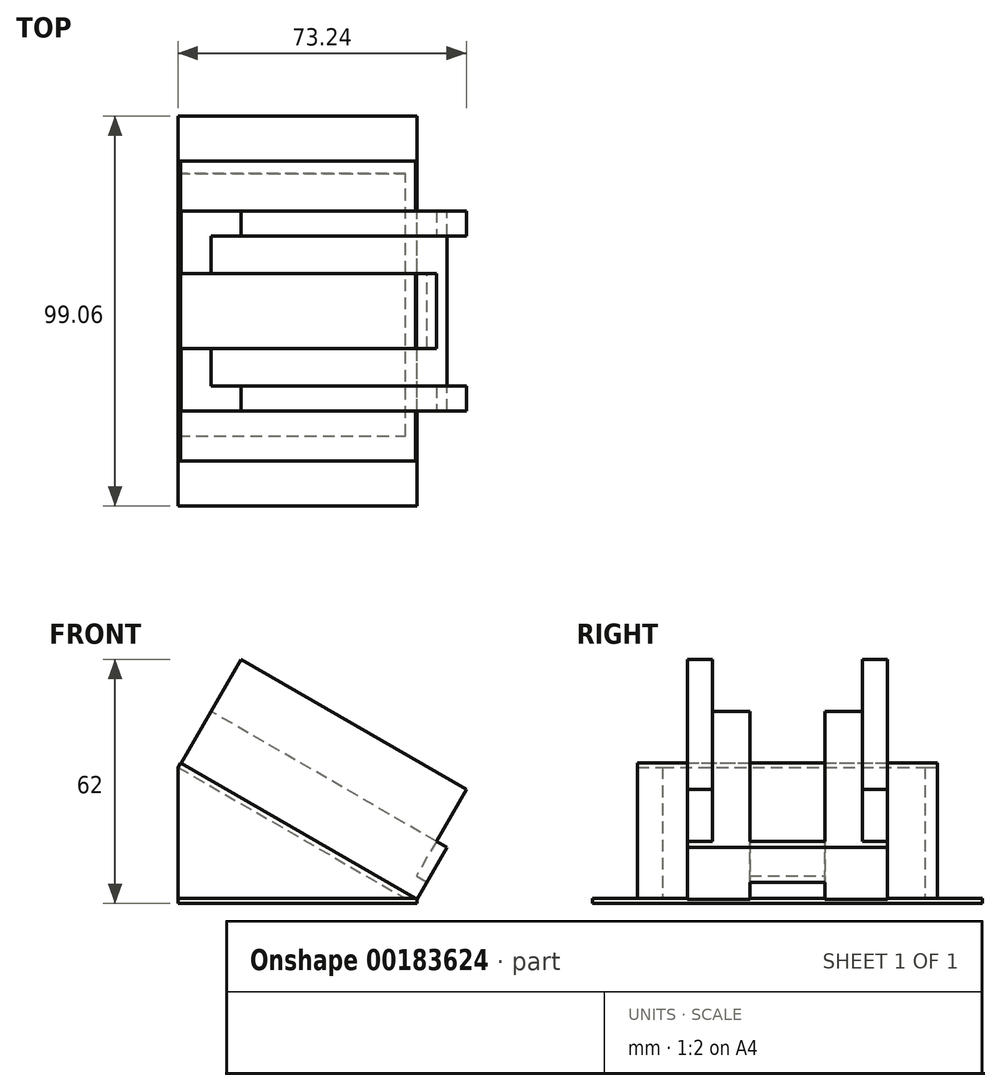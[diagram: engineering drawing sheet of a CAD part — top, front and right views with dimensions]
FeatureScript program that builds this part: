
annotation { "Feature Type Name" : "Feature", "Feature Type Description" : "" }
export const myFeature = defineFeature(function(context is Context, id is Id, definition is map)
    precondition{}
    {
        {
            var Q0;
            Q0=qCreatedBy(makeId("Front.planeOp"),FACE);
            var sketch = newSketch(context, id + "F0", { "sketchPlane" : qUnion([Q0])});
            skLineSegment(sketch, "E0", {"start": v(0, 0) * mm, "end": v(-60.11, 34.7) * mm});
            skLineSegment(sketch, "E1", {"start": v(-60.11, 34.7) * mm, "end": v(-60.75, 33.6) * mm});
            skLineSegment(sketch, "E2", {"start": v(-60.75, 33.6) * mm, "end": v(-0.8, -1) * mm});
            skLineSegment(sketch, "E3", {"start": v(-0.8, -1) * mm, "end": v(0, 0) * mm});
            skSolve(sketch);
        }
        {
            var Q0;
            Q0=qSketchRegion(id+"F0",true);
            extrude(context, id + "F1", {"entities" : qUnion([Q0]), "endBound" : BoundingType.SYMMETRIC, "depth" : 76.2 * mm});
        }
        {
            var Q0;
            Q0=makeQuery(id+"F1.opExtrude","SWEPT_FACE",FACE,{"disambiguationData":[OSD([sQuery(id+"F0.wireOp",EDGE,"E0")])]});
            var sketch = newSketch(context, id + "F2", { "sketchPlane" : qUnion([Q0])});
            skLineSegment(sketch, "E4.bottom", {"start": v(-3.18, 25.4) * mm, "end": v(0, 25.4) * mm});
            skLineSegment(sketch, "E4.top", {"start": v(-3.17, -25.4) * mm, "end": v(0, -25.4) * mm});
            skLineSegment(sketch, "E4.left", {"start": v(-3.18, 25.4) * mm, "end": v(-3.18, -25.4) * mm});
            skLineSegment(sketch, "E4.right", {"start": v(0, 25.4) * mm, "end": v(0, -25.4) * mm});
            skLineSegment(sketch, "E5.bottom", {"start": v(-3.18, 9.53) * mm, "end": v(-69.22, 9.53) * mm});
            skLineSegment(sketch, "E5.top", {"start": v(-3.17, -9.52) * mm, "end": v(-69.22, -9.53) * mm});
            skLineSegment(sketch, "E5.left", {"start": v(-3.18, 9.53) * mm, "end": v(-3.18, -9.52) * mm});
            skLineSegment(sketch, "E5.right", {"start": v(-69.22, 9.53) * mm, "end": v(-69.22, -9.53) * mm});
            skLineSegment(sketch, "E6.bottom", {"start": v(-3.18, 19.05) * mm, "end": v(-69.22, 19.05) * mm});
            skLineSegment(sketch, "E6.top", {"start": v(-3.17, -19.05) * mm, "end": v(-69.22, -19.05) * mm});
            skLineSegment(sketch, "E6.left", {"start": v(-3.18, 19.05) * mm, "end": v(-3.18, -19.05) * mm});
            skLineSegment(sketch, "E6.right", {"start": v(-69.22, 19.05) * mm, "end": v(-69.22, -19.05) * mm});
            skLineSegment(sketch, "E7.bottom", {"start": v(-3.18, 25.4) * mm, "end": v(-69.22, 25.4) * mm});
            skLineSegment(sketch, "E7.top", {"start": v(-3.17, -25.4) * mm, "end": v(-69.21, -25.4) * mm});
            skLineSegment(sketch, "E7.right", {"start": v(-69.22, 25.4) * mm, "end": v(-69.21, -25.4) * mm});
            skSolve(sketch);
        }
        {
            var Q0;
            {var subQ0=sQuery(id+"F2.wireOp",EDGE,"E5.top");Q0=makeQuery(id+"F2.imprint","IMPRINT",FACE,{"disambiguationData":[TD([[makeQuery(id+"F2.imprint","IMPRINT",EDGE,{"derivedFrom":subQ0}),1.0]])]});}
            var Q1;
            {var subQ0=sQuery(id+"F2.wireOp",EDGE,"E5.bottom");Q1=makeQuery(id+"F2.imprint","IMPRINT",FACE,{"disambiguationData":[TD([[makeQuery(id+"F2.imprint","IMPRINT",EDGE,{"derivedFrom":subQ0}),-1.0]])]});}
            extrude(context, id + "F3", {"entities" : qUnion([Q0, Q1]), "operationType" : NewBodyOperationType.ADD, "depth" : 15.24 * mm});
        }
        {
            var Q0;
            {var subQ0=sQuery(id+"F2.wireOp",EDGE,"E6.top");Q0=makeQuery(id+"F2.imprint","IMPRINT",FACE,{"disambiguationData":[TD([[makeQuery(id+"F2.imprint","IMPRINT",EDGE,{"derivedFrom":subQ0}),1.0]])]});}
            var Q1;
            {var subQ0=sQuery(id+"F2.wireOp",EDGE,"E6.bottom");Q1=makeQuery(id+"F2.imprint","IMPRINT",FACE,{"disambiguationData":[TD([[makeQuery(id+"F2.imprint","IMPRINT",EDGE,{"derivedFrom":subQ0}),-1.0]])]});}
            extrude(context, id + "F4", {"entities" : qUnion([Q0, Q1]), "operationType" : NewBodyOperationType.ADD, "depth" : 30.48 * mm});
        }
        {
            var Q0;
            {var subQ4=sQuery(id+"F2.wireOp",EDGE,"E4.bottom");Q0=makeQuery(id+"F2.imprint","IMPRINT",FACE,{"disambiguationData":[TD([[makeQuery(id+"F2.imprint","IMPRINT",EDGE,{"derivedFrom":subQ4}),-1.0]])]});}
            extrude(context, id + "F5", {"entities" : qUnion([Q0]), "operationType" : NewBodyOperationType.ADD, "depth" : 15.24 * mm});
        }
        {
            var Q0;
            Q0=makeQuery(id+"F5.opExtrude","SWEPT_FACE",FACE,{"disambiguationData":[OSD([sQuery(id+"F2.wireOp",EDGE,"E4.right")])]});
            var sketch = newSketch(context, id + "F6", { "sketchPlane" : qUnion([Q0])});
            skLineSegment(sketch, "E8.bottom", {"start": v(-9.53, 5.08) * mm, "end": v(9.52, 5.08) * mm});
            skLineSegment(sketch, "E8.top", {"start": v(-9.53, 0) * mm, "end": v(9.52, 0) * mm});
            skLineSegment(sketch, "E8.left", {"start": v(-9.53, 5.08) * mm, "end": v(-9.53, 0) * mm});
            skLineSegment(sketch, "E8.right", {"start": v(9.52, 5.08) * mm, "end": v(9.52, 0) * mm});
            skSolve(sketch);
        }
        {
            var Q0;
            Q0=qSketchRegion(id+"F6",true);
            extrude(context, id + "F7", {"entities" : qUnion([Q0]), "operationType" : NewBodyOperationType.REMOVE, "oppositeDirection" : true, "depth" : 3.17 * mm});
        }
        {
            var Q0;
            Q0=makeQuery(id+"F1.opExtrude","CAP_FACE",FACE,{"disambiguationData":[OSD([sQuery(id+"F0.wireOp",EDGE,"E0"),sQuery(id+"F0.wireOp",EDGE,"E1"),sQuery(id+"F0.wireOp",EDGE,"E2"),sQuery(id+"F0.wireOp",EDGE,"E3")])],"isStart":false});
            var sketch = newSketch(context, id + "F8", { "sketchPlane" : qUnion([Q0])});
            skLineSegment(sketch, "E9", {"start": v(-0.8, -1) * mm, "end": v(-60.75, -1) * mm});
            skLineSegment(sketch, "E10", {"start": v(-60.75, -1) * mm, "end": v(-60.75, 33.6) * mm});
            skLineSegment(sketch, "E11", {"start": v(-60.75, 33.6) * mm, "end": v(-0.8, -1) * mm});
            skSolve(sketch);
        }
        {
            var Q0;
            Q0=qSketchRegion(id+"F8",true);
            extrude(context, id + "F9", {"entities" : qUnion([Q0]), "operationType" : NewBodyOperationType.ADD, "oppositeDirection" : true, "depth" : 6.35 * mm});
        }
        {
            var Q0;
            Q0=makeQuery(id+"F1.opExtrude","CAP_FACE",FACE,{"disambiguationData":[OSD([sQuery(id+"F0.wireOp",EDGE,"E0"),sQuery(id+"F0.wireOp",EDGE,"E1"),sQuery(id+"F0.wireOp",EDGE,"E2"),sQuery(id+"F0.wireOp",EDGE,"E3")])],"isStart":true});
            var sketch = newSketch(context, id + "F10", { "sketchPlane" : qUnion([Q0])});
            skLineSegment(sketch, "E12", {"start": v(0.8, -1) * mm, "end": v(60.7, -1) * mm});
            skLineSegment(sketch, "E13", {"start": v(60.7, -1) * mm, "end": v(60.75, 33.6) * mm});
            skLineSegment(sketch, "E14", {"start": v(60.75, 33.6) * mm, "end": v(0.8, -1) * mm});
            skSolve(sketch);
        }
        {
            var Q0;
            Q0=qSketchRegion(id+"F10",true);
            extrude(context, id + "F11", {"entities" : qUnion([Q0]), "operationType" : NewBodyOperationType.ADD, "oppositeDirection" : true, "depth" : 3.17 * mm});
        }
        {
            var Q0;
            Q0=makeQuery(id+"F9.opExtrude","SWEPT_FACE",FACE,{"disambiguationData":[OSD([sQuery(id+"F8.wireOp",EDGE,"E9")])]});
            var sketch = newSketch(context, id + "F12", { "sketchPlane" : qUnion([Q0])});
            skLineSegment(sketch, "E15.bottom", {"start": v(-60.75, 49.53) * mm, "end": v(0, 49.53) * mm});
            skLineSegment(sketch, "E15.top", {"start": v(-60.75, -49.53) * mm, "end": v(0, -49.53) * mm});
            skLineSegment(sketch, "E15.left", {"start": v(-60.75, 49.53) * mm, "end": v(-60.75, -49.53) * mm});
            skLineSegment(sketch, "E15.right", {"start": v(0, 49.53) * mm, "end": v(0, -49.53) * mm});
            skLineSegment(sketch, "E16.left", {"start": v(0, 9.53) * mm, "end": v(0, -9.52) * mm});
            skSolve(sketch);
        }
        {
            var Q0;
            {var subQ2=sQuery(id+"F12.wireOp",EDGE,"E15.bottom");Q0=makeQuery(id+"F12.imprint","IMPRINT",FACE,{"disambiguationData":[TD([[makeQuery(id+"F12.imprint","IMPRINT",EDGE,{"derivedFrom":subQ2}),-1.0]])]});}
            extrude(context, id + "F13", {"entities" : qUnion([Q0]), "operationType" : NewBodyOperationType.ADD, "oppositeDirection" : true, "depth" : 1.27 * mm});
        }
    });
